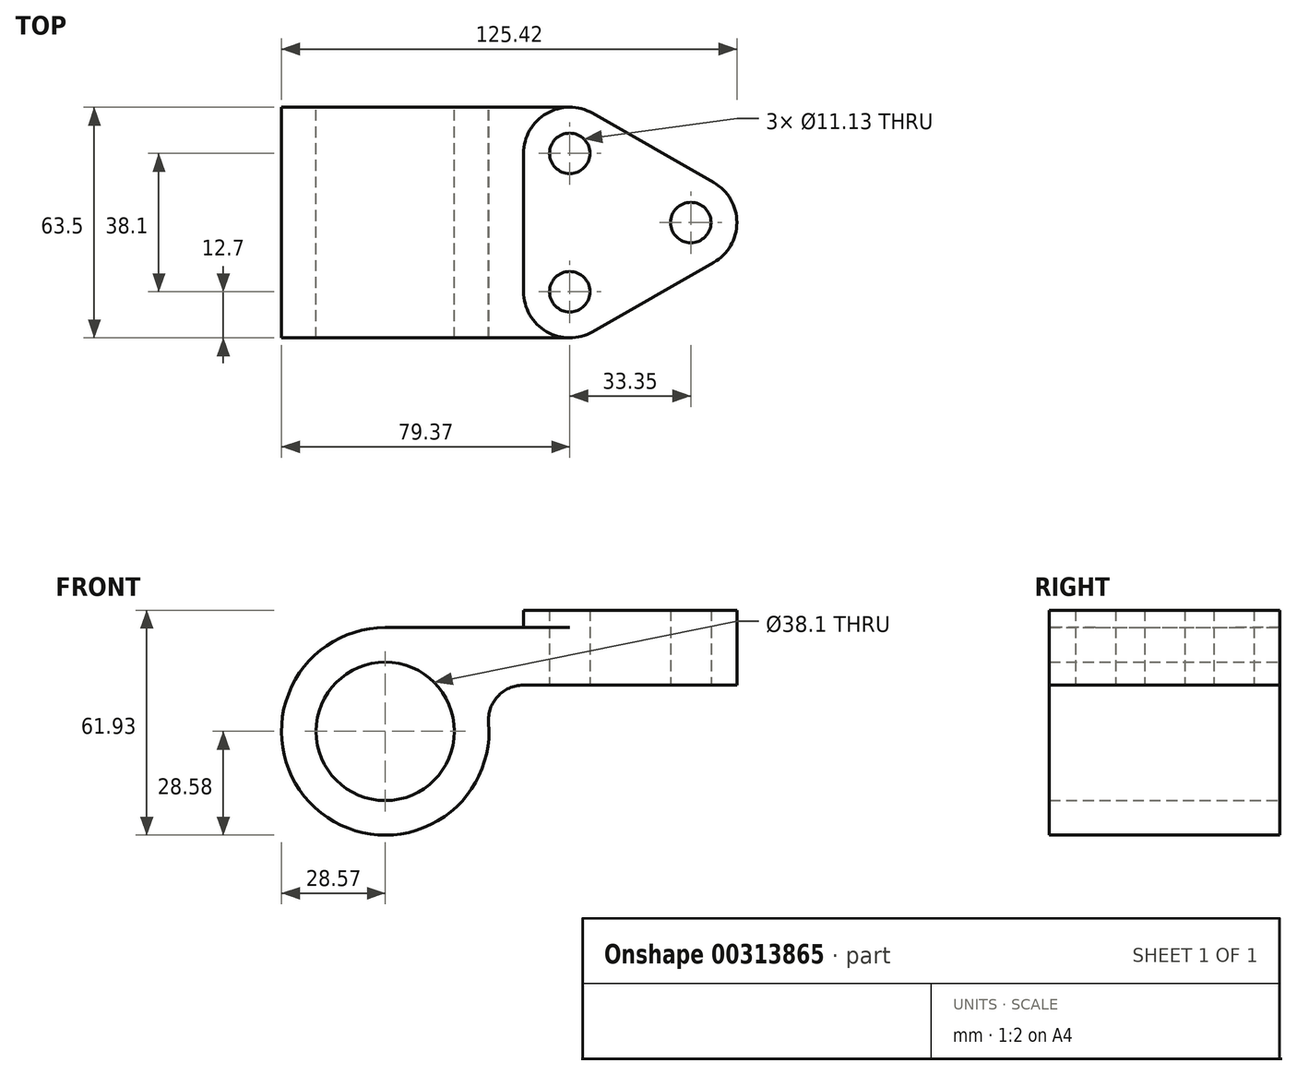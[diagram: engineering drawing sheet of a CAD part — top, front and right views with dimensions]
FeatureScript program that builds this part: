
annotation { "Feature Type Name" : "Feature", "Feature Type Description" : "" }
export const myFeature = defineFeature(function(context is Context, id is Id, definition is map)
    precondition{}
    {
        {
            var Q0;
            Q0=qCreatedBy(makeId("Front.planeOp"),FACE);
            var sketch = newSketch(context, id + "F0", { "sketchPlane" : qUnion([Q0])});
            skCircle(sketch, "E0", {"center": v(0, 0) * mm, "radius": 19.05 * mm});
            skArc(sketch, "E1", {"start": v(0, 28.58) * mm, "mid": v(-19.35, -21.03) * mm, "end": v(28.48, 2.38) * mm});
            skLineSegment(sketch, "E2", {"start": v(0, 28.58) * mm, "end": v(50.8, 28.58) * mm});
            skLineSegment(sketch, "E3", {"start": v(50.8, 28.58) * mm, "end": v(50.8, 12.7) * mm});
            skPoint(sketch, "E4.orphan", {"position": v(28.58, 0) * mm});
            skLineSegment(sketch, "E5", {"start": v(50.8, 12.7) * mm, "end": v(37.97, 12.7) * mm});
            skArc(sketch, "E6", {"start": v(37.97, 12.7) * mm, "mid": v(30.96, 9.62) * mm, "end": v(28.48, 2.38) * mm});
            skSolve(sketch);
        }
        {
            var Q0;
            Q0 = qSketchRegion(id + "F0", true);
            extrude(context, id + "F1", {"entities" : qUnion([Q0]), "depth" : 63.5 * mm});
        }
        {
            var Q0;
            Q0=qCreatedBy(makeId("Top.planeOp"),FACE);
            cPlane(context, id + "F2", {"entities" : qUnion([Q0]), "cplaneType" : CPlaneType.OFFSET, "offset" : 28.57 * mm, "width" : 152.4 * mm, "height" : 152.4 * mm});
        }
        {
            var Q0;
            Q0=qCreatedBy(id+"F2.planeOp",FACE);
            var sketch = newSketch(context, id + "F3", { "sketchPlane" : qUnion([Q0])});
            skLineSegment(sketch, "E7", {"start": v(0, -31.75) * mm, "end": v(127, -31.75) * mm, "construction": true});
            skCircle(sketch, "E8", {"center": v(50.8, -12.7) * mm, "radius": 5.56 * mm});
            skCircle(sketch, "E9", {"center": v(50.8, -50.8) * mm, "radius": 5.56 * mm});
            skCircle(sketch, "E10", {"center": v(84.15, -31.75) * mm, "radius": 5.56 * mm});
            skLineSegment(sketch, "E11", {"start": v(38.1, -12.7) * mm, "end": v(38.1, -50.8) * mm});
            skLineSegment(sketch, "E12", {"start": v(90.45, -42.78) * mm, "end": v(57.1, -61.83) * mm});
            skArc(sketch, "E13", {"start": v(90.45, -42.78) * mm, "mid": v(96.85, -31.75) * mm, "end": v(90.45, -20.72) * mm});
            skArc(sketch, "E14", {"start": v(38.1, -50.8) * mm, "mid": v(44.42, -61.78) * mm, "end": v(57.1, -61.83) * mm});
            skArc(sketch, "E15", {"start": v(57.1, -1.67) * mm, "mid": v(44.42, -1.72) * mm, "end": v(38.1, -12.7) * mm});
            skLineSegment(sketch, "E16", {"start": v(90.45, -20.72) * mm, "end": v(57.1, -1.67) * mm});
            skSolve(sketch);
        }
        {
            var Q0;
            Q0 = qSketchRegion(id + "F3", true);
            extrude(context, id + "F4", {"entities" : qUnion([Q0]), "operationType" : NewBodyOperationType.ADD, "depth" : 4.78 * mm, "hasSecondDirection" : true, "secondDirectionOppositeDirection" : true, "secondDirectionDepth" : 15.88 * mm});
        }
        {
            var Q0;
            Q0=makeQuery(id+"F4.opExtrude","CAP_FACE",FACE,{"disambiguationData":[OSD([sQuery(id+"F3.wireOp",EDGE,"E8"),sQuery(id+"F3.wireOp",EDGE,"E9"),sQuery(id+"F3.wireOp",EDGE,"E10"),sQuery(id+"F3.wireOp",EDGE,"E11"),sQuery(id+"F3.wireOp",EDGE,"E12"),sQuery(id+"F3.wireOp",EDGE,"E13"),sQuery(id+"F3.wireOp",EDGE,"E14"),sQuery(id+"F3.wireOp",EDGE,"E15"),sQuery(id+"F3.wireOp",EDGE,"E16")])],"isStart":false});
            var sketch = newSketch(context, id + "F5", { "sketchPlane" : qUnion([Q0])});
            skCircle(sketch, "E17", {"center": v(50.8, -12.7) * mm, "radius": 5.56 * mm});
            skCircle(sketch, "E18", {"center": v(50.8, -50.8) * mm, "radius": 5.56 * mm});
            skSolve(sketch);
        }
        {
            var Q0;
            Q0 = qSketchRegion(id + "F5", true);
            extrude(context, id + "F6", {"entities" : qUnion([Q0]), "operationType" : NewBodyOperationType.REMOVE, "endBound" : BoundingType.THROUGH_ALL, "oppositeDirection" : true, "depth" : 25.4 * mm});
        }
    });
